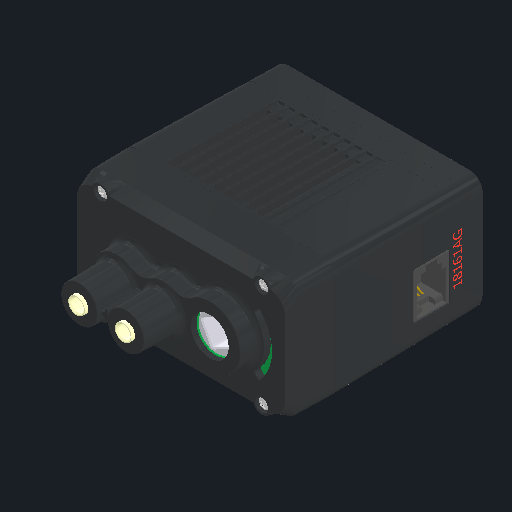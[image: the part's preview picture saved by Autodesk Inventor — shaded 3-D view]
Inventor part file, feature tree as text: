
AUTODESK INVENTOR PART (.ipt)
format: ipt  version: 2024 (Build 280153000, 153)  size: 8,712,192 bytes
history: native  units: in
note: dims shown in document units (in); Inventor stores cm internally (conversion verified against a paired STEP export)
features: other x15, extrude x2, sketch x2
ambient origin geometry x8: Origin, YZ Plane, XZ Plane, XY Plane, X Axis, Y Axis, Z Axis, Center Point
bodies: Solid1 (feature_tree), Solid2 (feature_tree), Solid4 (feature_tree), Solid6 (feature_tree), Solid7 (feature_tree), Solid8 (feature_tree), Solid9 (feature_tree), Solid14 (feature_tree), Solid16 (feature_tree), Solid17 (feature_tree), Solid18 (feature_tree), Solid19 (feature_tree), Solid20 (feature_tree), Solid21 (feature_tree), Solid22 (feature_tree)
feature tree (19):
  extrude  "Extrusion1"  TaperAngle=0.0deg  [1 undecoded]
  extrude  "Extrusion2"  Depth=0.1969in
  sketch  "Sketch1"  dims[d4=0.0in d5=0.0in]
  sketch  "Sketch2"  dims[d48=0.0197in d73=0.1969in d74=0.0148in d75=0.0591in d121=0.0984in d126=0.0394in d131=0.002in d132=0.0in d133=0.002in d134=0.0in]
  other  "276-4840-001 Rev38_1:1"
  other  "276-4840-005 Rev27_2:1"
  other  "276-4840-902 Rev2_24:1"
  other  "276-4840-004 Rev16_4:1"
  other  "276-4840-015 Rev7_5:1"
  other  "276-4840-015 Rev7_6:1"
  other  "276-4840-015 Rev7_7:1"
  other  "276-4840-003 Rev27_12:1"
  other  "276-4840-018 Rev6_18:1"
  other  "276-4840-059 Rev2_19:1"
  other  "276-4840-062 Rev1_20:1"
  other  "276-4840-062 Rev1_21:1"
  other  "276-4840-062 Rev1_22:1"
  other  "276-4840-043 Rev8_14:1"
  other  "276-4840-043 Rev8_15:1"
note: 1 required parameter value undecoded (feature->parameter linkage not recoverable at this tier; creation-order binding heuristic only, values carry confidence <= 0.55)
